# Revit family: Shower-Shower_Door-KOHLER-ARTIFACTS-K-701727_1
name_source: partatom
category: Specialty Equipment
revit_build: Autodesk Revit 2017 (Build: 20160225_1515(x64)
units: mm (PartAtom-declared; Revit-internal decimal feet)

## family parameters
Cut with Voids When Loaded = No
Host = Face
OmniClass Number = 23.31.17.17
OmniClass Title = Shower Enclosures
Part Type = Normal
Room Calculation Point = No
Round Connector Dimension = Use Diameter
Shared = No

## types (4) — shared parameters
ADA Compliant = No
Assembly Code = C1030200
Date Modified = 12/21/2021
Default Elevation = 4"
Description = 3/8 SLIDER 80 X 45-1/4 TO 46 1/4 INCH
Height = 80 7/8"
Length = 6 3/16"
Manufacturer = KOHLER Co.
Master Format 2014 = 10 28 19.16
Master Format 2014 Name = Shower Doors
Material = Premium Metal Construction
Product Documentation Link = https://www.us.kohler.com
Product Name = ARTIFACTS
Product Page URL = http://www.us.kohler.com
URL = http://www.us.kohler.com
WaterSense Certified = No

## per-type parameters (varying)
| type | Finish | Model | Type |
| 2BZ-Oil Rubbed Bronze | Kohler-Metal-2BZ-Oil_Rubbed_Bronze | K-701727-10L-2BZ | 1 |
| BN-Vibrant Brushed Nickel | Kohler-Metal-BN-Vibrant_Brushed_Nickel | K-701727-10L-BN | 2 |
| CP-Polished Chrome | Kohler-Metal-CP-Polished_Chrome | K-701727-10L-CP | 3 |
| SN-Vibrant Polished Nickel | Kohler-Metal-SN-Vibrant_Polished_Nickel | K-701727-10L-SN | 4 |

## geometry (parser evidence)
native form markers: Sweep x5
no freeform markers — native parametric forms only
